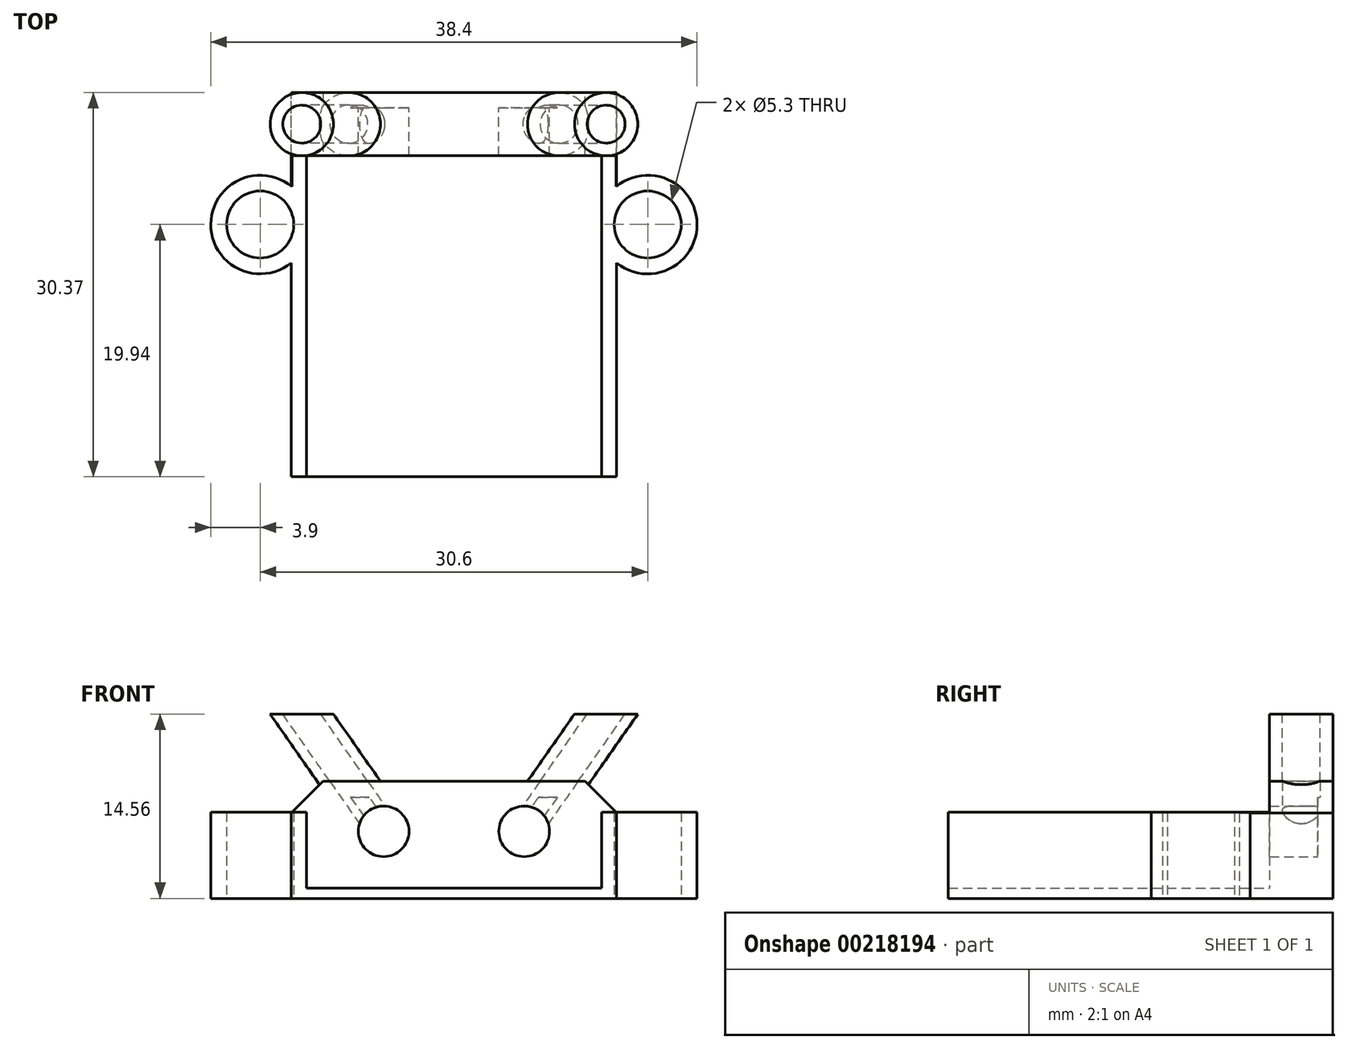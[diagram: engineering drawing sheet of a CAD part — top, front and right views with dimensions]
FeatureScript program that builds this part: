
annotation { "Feature Type Name" : "Feature", "Feature Type Description" : "" }
export const myFeature = defineFeature(function(context is Context, id is Id, definition is map)
    precondition{}
    {
        {
            var Q0;
            Q0=qCreatedBy(makeId("Top.planeOp"),FACE);
            var sketch = newSketch(context, id + "F0", { "sketchPlane" : qUnion([Q0])});
            skCircle(sketch, "E0", {"center": v(15.3, 9.57) * mm, "radius": 2.65 * mm});
            skCircle(sketch, "E1", {"center": v(-15.3, 9.57) * mm, "radius": 2.65 * mm});
            skArc(sketch, "E2", {"start": v(-12.85, 12.6) * mm, "mid": v(-19.2, 9.57) * mm, "end": v(-12.85, 6.54) * mm});
            skCircle(sketch, "E3", {"center": v(15.3, 9.57) * mm, "radius": 3.9 * mm});
            skLineSegment(sketch, "E4", {"start": v(-11.65, 18.8) * mm, "end": v(11.65, 18.8) * mm});
            skLineSegment(sketch, "E5.3", {"start": v(-14.24, 12) * mm, "end": v(-14.24, 12.03) * mm});
            skLineSegment(sketch, "E5.5", {"start": v(-11.65, -10.37) * mm, "end": v(11.65, -10.37) * mm});
            skPoint(sketch, "E6.end.orphan", {"position": v(0, 20) * mm});
            skLineSegment(sketch, "E7", {"start": v(-11.65, -10.37) * mm, "end": v(-11.65, 18.8) * mm});
            skLineSegment(sketch, "E8", {"start": v(11.65, -10.37) * mm, "end": v(11.65, 18.8) * mm});
            skLineSegment(sketch, "E9.0", {"start": v(12.85, -10.37) * mm, "end": v(12.85, 20) * mm});
            skLineSegment(sketch, "E9.1", {"start": v(-12.85, 20) * mm, "end": v(12.85, 20) * mm});
            skLineSegment(sketch, "E9.2", {"start": v(-12.85, -10.37) * mm, "end": v(-12.85, 20) * mm});
            skLineSegment(sketch, "E10", {"start": v(-12.85, 15) * mm, "end": v(12.85, 15) * mm});
            skLineSegment(sketch, "E11", {"start": v(-12.85, -10.37) * mm, "end": v(-11.65, -10.37) * mm});
            skLineSegment(sketch, "E12", {"start": v(11.65, -10.37) * mm, "end": v(12.85, -10.37) * mm});
            skArc(sketch, "E13.trimOffspring", {"start": v(-11.65, 8.2) * mm, "mid": v(-11.4, 9.57) * mm, "end": v(-11.65, 10.95) * mm});
            skSolve(sketch);
        }
        {
            var Q0;
            {var subQ0=sQuery(id+"F0.wireOp",EDGE,"E4");Q0=makeQuery(id+"F0.imprint","IMPRINT",FACE,{"disambiguationData":[TD([[makeQuery(id+"F0.imprint","IMPRINT",EDGE,{"derivedFrom":subQ0}),1.0]])]});}
            var Q1;
            {var subQ0=sQuery(id+"F0.wireOp",EDGE,"E4");Q1=makeQuery(id+"F0.imprint","IMPRINT",FACE,{"disambiguationData":[TD([[makeQuery(id+"F0.imprint","IMPRINT",EDGE,{"derivedFrom":subQ0}),-1.0]])]});}
            extrude(context, id + "F1", {"entities" : qUnion([Q0, Q1]), "depth" : 9.25 * mm});
        }
        {
            var Q0;
            Q0=makeQuery(id+"F1.opExtrude","SWEPT_FACE",FACE,{"disambiguationData":[OSD([sQuery(id+"F0.wireOp",EDGE,"E9.1")])]});
            var sketch = newSketch(context, id + "F2", { "sketchPlane" : qUnion([Q0])});
            skLineSegment(sketch, "E14", {"start": v(-5.55, 0) * mm, "end": v(-5.55, 5.3) * mm});
            skCircle(sketch, "E15", {"center": v(-5.55, 5.3) * mm, "radius": 2 * mm});
            skLineSegment(sketch, "E16", {"start": v(5.55, 0) * mm, "end": v(5.55, 5.3) * mm});
            skCircle(sketch, "E17", {"center": v(5.55, 5.3) * mm, "radius": 2 * mm});
            skLineSegment(sketch, "E18", {"start": v(5.55, 5.3) * mm, "end": v(8.3, 9.23) * mm});
            skLineSegment(sketch, "E19", {"start": v(-5.55, 5.3) * mm, "end": v(-8.3, 9.23) * mm});
            skLineSegment(sketch, "E20", {"start": v(8.3, 9.23) * mm, "end": v(12.03, 14.56) * mm});
            skLineSegment(sketch, "E21", {"start": v(-8.3, 9.23) * mm, "end": v(-12.03, 14.56) * mm});
            skSolve(sketch);
        }
        {
            var Q0;
            Q0=makeQuery(id+"F2.imprint","IMPRINT",FACE,{"disambiguationData":[TD([[makeQuery(id+"F2.imprint","IMPRINT",EDGE,{"derivedFrom":sQuery(id+"F2.wireOp",EDGE,"E17")}),1.0]])]});
            var Q1;
            Q1=makeQuery(id+"F2.imprint","IMPRINT",FACE,{"disambiguationData":[TD([[makeQuery(id+"F2.imprint","IMPRINT",EDGE,{"derivedFrom":sQuery(id+"F2.wireOp",EDGE,"E15")}),1.0]])]});
            extrude(context, id + "F3", {"entities" : qUnion([Q0, Q1]), "operationType" : NewBodyOperationType.REMOVE, "oppositeDirection" : true, "depth" : 7 * mm});
        }
        {
            var Q0;
            Q0=makeQuery(id+"F1.opExtrude","CAP_FACE",FACE,{"disambiguationData":[OSD([sQuery(id+"F0.wireOp",EDGE,"E2"),sQuery(id+"F0.wireOp",EDGE,"E3"),sQuery(id+"F0.wireOp",EDGE,"E9.0"),sQuery(id+"F0.wireOp",EDGE,"E9.1"),sQuery(id+"F0.wireOp",EDGE,"E9.2"),sQuery(id+"F0.wireOp",EDGE,"E10")])],"isStart":false});
            var sketch = newSketch(context, id + "F4", { "sketchPlane" : qUnion([Q0])});
            skCircle(sketch, "E22", {"center": v(-8.3, 17.5) * mm, "radius": 2.5 * mm});
            skCircle(sketch, "E23", {"center": v(8.3, 17.5) * mm, "radius": 2.5 * mm});
            skCircle(sketch, "E24", {"center": v(-8.3, 17.5) * mm, "radius": 1.5 * mm});
            skCircle(sketch, "E25", {"center": v(8.3, 17.5) * mm, "radius": 1.5 * mm});
            skLineSegment(sketch, "E26.0", {"start": v(-8.3, 20) * mm, "end": v(-8.32, 20) * mm});
            skPoint(sketch, "E27.orphan", {"position": v(-7.55, 15) * mm});
            skPoint(sketch, "E28.end.orphan", {"position": v(3.55, 15) * mm});
            skLineSegment(sketch, "E29.trimOffspring", {"start": v(8.3, 20) * mm, "end": v(8.32, 20) * mm});
            skSolve(sketch);
        }
        {
            var Q0;
            Q0=makeQuery(id+"F4.imprint","IMPRINT",FACE,{"disambiguationData":[TD([[makeQuery(id+"F4.imprint","IMPRINT",EDGE,{"derivedFrom":sQuery(id+"F4.wireOp",EDGE,"E24")}),-1.0]])]});
            var Q1;
            Q1=sQuery(id+"F2.wireOp",EDGE,"E20");
            sweep(context, id + "F5", {"operationType" : NewBodyOperationType.ADD, "profiles" : qUnion([Q0]), "path" : qUnion([Q1])});
        }
        {
            var Q0;
            Q0=makeQuery(id+"F4.imprint","IMPRINT",FACE,{"disambiguationData":[TD([[makeQuery(id+"F4.imprint","IMPRINT",EDGE,{"derivedFrom":sQuery(id+"F4.wireOp",EDGE,"E25")}),-1.0]])]});
            var Q1;
            Q1=sQuery(id+"F2.wireOp",EDGE,"E21");
            sweep(context, id + "F6", {"operationType" : NewBodyOperationType.ADD, "profiles" : qUnion([Q0]), "path" : qUnion([Q1])});
        }
        {
            var Q0;
            Q0=makeQuery(id+"F4.imprint","IMPRINT",FACE,{"disambiguationData":[TD([[makeQuery(id+"F4.imprint","IMPRINT",EDGE,{"derivedFrom":sQuery(id+"F4.wireOp",EDGE,"E24")}),1.0]])]});
            var Q1;
            Q1=sQuery(id+"F2.wireOp",EDGE,"E18");
            sweep(context, id + "F7", {"operationType" : NewBodyOperationType.REMOVE, "profiles" : qUnion([Q0]), "path" : qUnion([Q1])});
        }
        {
            var Q0;
            Q0=makeQuery(id+"F4.imprint","IMPRINT",FACE,{"disambiguationData":[TD([[makeQuery(id+"F4.imprint","IMPRINT",EDGE,{"derivedFrom":sQuery(id+"F4.wireOp",EDGE,"E25")}),1.0]])]});
            var Q1;
            Q1=sQuery(id+"F2.wireOp",EDGE,"E19");
            sweep(context, id + "F8", {"operationType" : NewBodyOperationType.REMOVE, "profiles" : qUnion([Q0]), "path" : qUnion([Q1])});
        }
        {
            var Q0;
            {var subQ10=sQuery(id+"F0.wireOp",EDGE,"E11");Q0=makeQuery(id+"F0.imprint","IMPRINT",FACE,{"disambiguationData":[TD([[makeQuery(id+"F0.imprint","IMPRINT",EDGE,{"derivedFrom":subQ10}),1.0]])]});}
            var Q1;
            {var subQ1=sQuery(id+"F0.wireOp",EDGE,"E2");Q1=makeQuery(id+"F0.imprint","IMPRINT",FACE,{"disambiguationData":[TD([[makeQuery(id+"F0.imprint","IMPRINT",EDGE,{"derivedFrom":subQ1}),1.0]])]});}
            var Q2;
            {var subQ5=sQuery(id+"F0.wireOp",EDGE,"E12");Q2=makeQuery(id+"F0.imprint","IMPRINT",FACE,{"disambiguationData":[TD([[makeQuery(id+"F0.imprint","IMPRINT",EDGE,{"derivedFrom":subQ5}),1.0]])]});}
            var Q3;
            {var subQ0=sQuery(id+"F0.wireOp",EDGE,"E9.0");var subQ5=sQuery(id+"F0.wireOp",EDGE,"E0");var subQ6=makeQuery(id+"F0.imprint","INTERSECT",VERTEX,{"disambiguationData":[OD(0.0)],"derivedFrom":[subQ5,subQ0]});Q3=makeQuery(id+"F0.imprint","IMPRINT",FACE,{"disambiguationData":[TD([[makeQuery(id+"F0.imprint","IMPRINT",EDGE,{"disambiguationData":[TD([[subQ6,1.0]])],"derivedFrom":subQ5}),-1.0]])]});}
            var Q4;
            {var subQ0=sQuery(id+"F0.wireOp",EDGE,"E9.0");var subQ1=sQuery(id+"F0.wireOp",EDGE,"E3");var subQ2=makeQuery(id+"F0.imprint","INTERSECT",VERTEX,{"disambiguationData":[OD(0.0)],"derivedFrom":[subQ1,subQ0]});Q4=makeQuery(id+"F0.imprint","IMPRINT",FACE,{"disambiguationData":[TD([[makeQuery(id+"F0.imprint","IMPRINT",EDGE,{"disambiguationData":[TD([[subQ2,-1.0]])],"derivedFrom":subQ1}),-1.0]])]});}
            var Q5;
            {var subQ0=sQuery(id+"F0.wireOp",EDGE,"E9.0");var subQ1=sQuery(id+"F0.wireOp",EDGE,"E0");var subQ2=makeQuery(id+"F0.imprint","INTERSECT",VERTEX,{"disambiguationData":[OD(0.0)],"derivedFrom":[subQ1,subQ0]});Q5=makeQuery(id+"F0.imprint","IMPRINT",FACE,{"disambiguationData":[TD([[makeQuery(id+"F0.imprint","IMPRINT",EDGE,{"disambiguationData":[TD([[subQ2,-1.0]])],"derivedFrom":subQ1}),-1.0]])]});}
            extrude(context, id + "F9", {"entities" : qUnion([Q0, Q1, Q2, Q3, Q4, Q5]), "operationType" : NewBodyOperationType.ADD, "depth" : 6.8 * mm});
        }
        {
            var Q0;
            {var subQ9=sQuery(id+"F0.wireOp",EDGE,"E5.5");Q0=makeQuery(id+"F0.imprint","IMPRINT",FACE,{"disambiguationData":[TD([[makeQuery(id+"F0.imprint","IMPRINT",EDGE,{"derivedFrom":subQ9}),1.0]])]});}
            var Q1;
            {var subQ0=sQuery(id+"F0.wireOp",EDGE,"E13.trimOffspring");Q1=makeQuery(id+"F0.imprint","IMPRINT",FACE,{"disambiguationData":[TD([[makeQuery(id+"F0.imprint","IMPRINT",EDGE,{"derivedFrom":subQ0}),1.0]])]});}
            var Q2;
            {var subQ0=sQuery(id+"F0.wireOp",EDGE,"E8");var subQ1=sQuery(id+"F0.wireOp",EDGE,"E3");var subQ2=makeQuery(id+"F0.imprint","INTERSECT",VERTEX,{"disambiguationData":[OD(0.0)],"derivedFrom":[subQ1,subQ0]});Q2=makeQuery(id+"F0.imprint","IMPRINT",FACE,{"disambiguationData":[TD([[makeQuery(id+"F0.imprint","IMPRINT",EDGE,{"disambiguationData":[TD([[subQ2,-1.0]])],"derivedFrom":subQ1}),1.0]])]});}
            extrude(context, id + "F10", {"entities" : qUnion([Q0, Q1, Q2]), "operationType" : NewBodyOperationType.ADD, "depth" : 0.8 * mm});
        }
        {
            var Q0;
            Q0=makeQuery(id+"F1.opExtrude","CAP_EDGE",EDGE,{"disambiguationData":[OSD([sQuery(id+"F0.wireOp",EDGE,"E9.0")])],"isStart":false});
            var Q1;
            Q1=makeQuery(id+"F1.opExtrude","CAP_EDGE",EDGE,{"disambiguationData":[OSD([sQuery(id+"F0.wireOp",EDGE,"E9.2")])],"isStart":false});
            chamfer(context, id + "F11", {"entities" : qUnion([Q0, Q1]), "width" : 2.5 * mm, "tangentPropagation" : true});
        }
        {
            var Q0;
            {var subQ1=sQuery(id+"F0.wireOp",EDGE,"E4");Q0=makeQuery(id+"F0.imprint","IMPRINT",FACE,{"disambiguationData":[TD([[makeQuery(id+"F0.imprint","IMPRINT",EDGE,{"derivedFrom":subQ1}),1.0]])]});}
            extrude(context, id + "F12", {"entities" : qUnion([Q0]), "operationType" : NewBodyOperationType.ADD, "depth" : 8 * mm});
        }
        {
            var Q0;
            Q0=makeQuery(id+"F12.opExtrude","CAP_EDGE",EDGE,{"disambiguationData":[OSD([sQuery(id+"F0.wireOp",EDGE,"E9.0")])],"isStart":false});
            var Q1;
            Q1=makeQuery(id+"F12.opExtrude","CAP_EDGE",EDGE,{"disambiguationData":[OSD([sQuery(id+"F0.wireOp",EDGE,"E9.2")])],"isStart":false});
            chamfer(context, id + "F13", {"entities" : qUnion([Q0, Q1]), "width" : 1.25 * mm, "tangentPropagation" : true});
        }
    });
